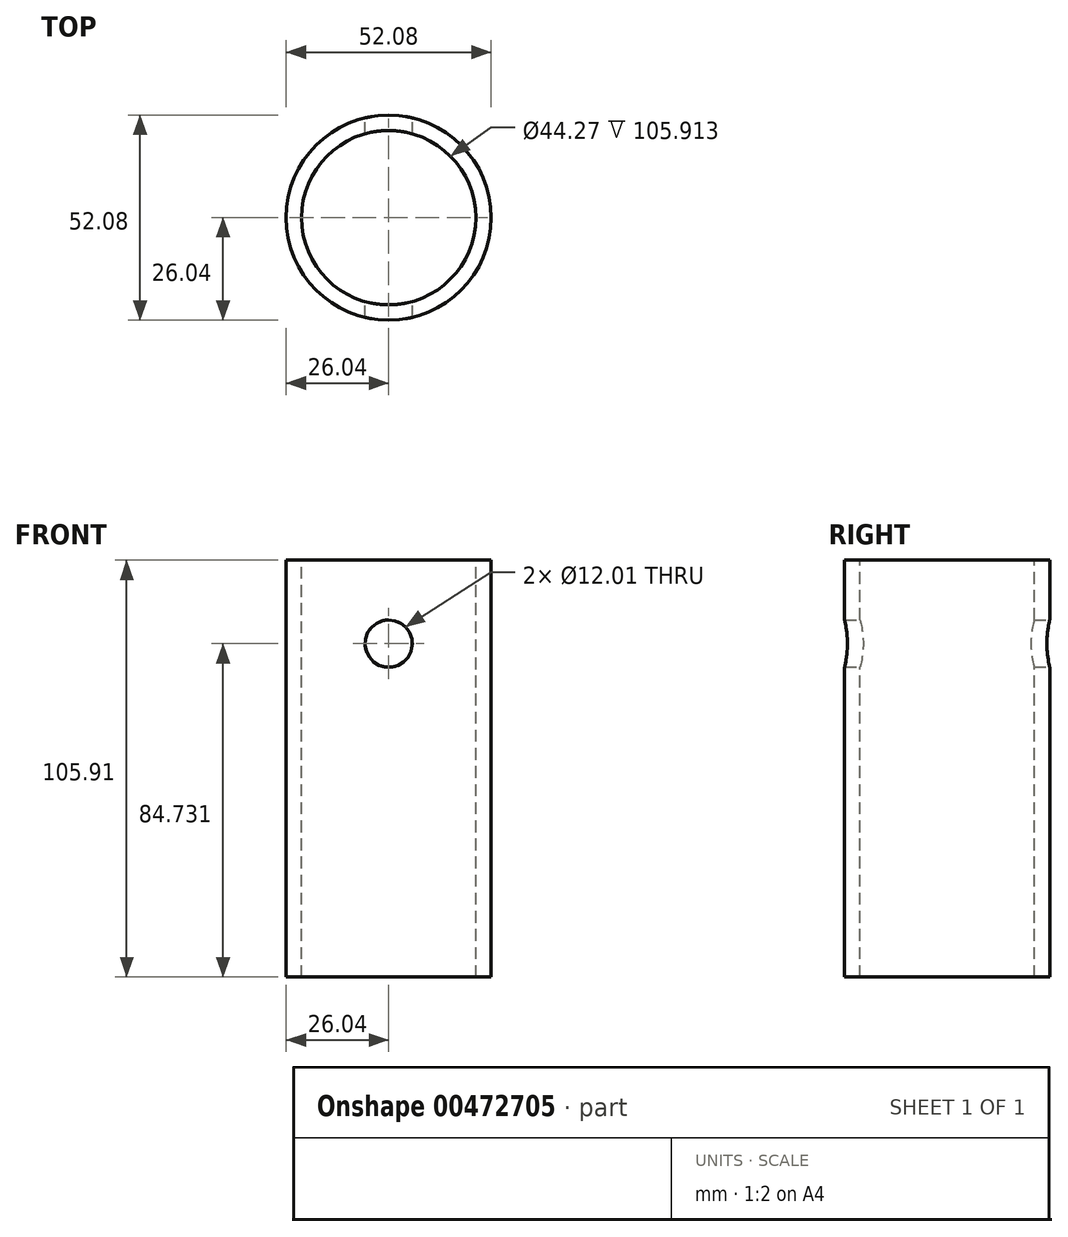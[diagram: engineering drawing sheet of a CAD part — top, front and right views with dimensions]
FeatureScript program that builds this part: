
annotation { "Feature Type Name" : "Feature", "Feature Type Description" : "" }
export const myFeature = defineFeature(function(context is Context, id is Id, definition is map)
    precondition{}
    {
        {
            var Q0;
            Q0=qCreatedBy(makeId("Top.planeOp"),FACE);
            var sketch = newSketch(context, id + "F0", { "sketchPlane" : qUnion([Q0])});
            skCircle(sketch, "E0", {"center": v(0, 0) * mm, "radius": 26.04 * mm});
            skSolve(sketch);
        }
        {
            var Q0;
            Q0 = qSketchRegion(id + "F0", true);
            extrude(context, id + "F1", {"entities" : qUnion([Q0]), "depth" : 105.9 * mm});
        }
        {
            var Q0;
            Q0=makeQuery(id+"F1.opExtrude","CAP_FACE",FACE,{"disambiguationData":[OSD([sQuery(id+"F0.wireOp",EDGE,"E0")])],"isStart":false});
            var sketch = newSketch(context, id + "F2", { "sketchPlane" : qUnion([Q0])});
            skSolve(sketch);
        }
        {
            var Q0;
            Q0=makeQuery(id+"F2.imprint","IMPRINT",FACE,{"disambiguationData":[TD([[makeQuery(id+"F2.imprint","IMPRINT",EDGE,{"derivedFrom":makeQuery(id+"F1.opExtrude","CAP_EDGE",EDGE,{"disambiguationData":[OSD([sQuery(id+"F0.wireOp",EDGE,"E0")])],"isStart":false})}),1.0]])]});
            var sketch = newSketch(context, id + "F3", { "sketchPlane" : qUnion([Q0])});
            skCircle(sketch, "E1", {"center": v(0, 0) * mm, "radius": 22.13 * mm});
            skSolve(sketch);
        }
        {
            var Q0;
            Q0 = qSketchRegion(id + "F3", true);
            var sketch = newSketch(context, id + "F4", { "sketchPlane" : qUnion([Q0])});
            skSolve(sketch);
        }
        {
            var Q0;
            Q0=makeQuery(id+"F2.imprint","IMPRINT",FACE,{"disambiguationData":[TD([[makeQuery(id+"F2.imprint","IMPRINT",EDGE,{"derivedFrom":makeQuery(id+"F1.opExtrude","CAP_EDGE",EDGE,{"disambiguationData":[OSD([sQuery(id+"F0.wireOp",EDGE,"E0")])],"isStart":false})}),1.0]])]});
            var Q1;
            Q1=makeQuery(id+"F3.imprint","IMPRINT",FACE,{"disambiguationData":[TD([[makeQuery(id+"F3.imprint","IMPRINT",EDGE,{"derivedFrom":sQuery(id+"F3.wireOp",EDGE,"E1")}),1.0]])]});
            extrude(context, id + "F5", {"entities" : qUnion([Q0, Q1]), "operationType" : NewBodyOperationType.ADD, "oppositeDirection" : true, "depth" : 88.55 * mm});
        }
        {
            var Q0;
            Q0=makeQuery(id+"F4.imprint","IMPRINT",FACE,{"disambiguationData":[TD([[makeQuery(id+"F4.imprint","IMPRINT",EDGE,{"derivedFrom":makeQuery(id+"F3.imprint","IMPRINT",EDGE,{"derivedFrom":sQuery(id+"F3.wireOp",EDGE,"E1")})}),1.0]])]});
            extrude(context, id + "F6", {"entities" : qUnion([Q0]), "operationType" : NewBodyOperationType.REMOVE, "oppositeDirection" : true, "depth" : 185.23 * mm});
        }
        {
            var Q0;
            Q0=qCreatedBy(makeId("Front.planeOp"),FACE);
            var sketch = newSketch(context, id + "F7", { "sketchPlane" : qUnion([Q0])});
            skCircle(sketch, "E2", {"center": v(0, 84.73) * mm, "radius": 6 * mm});
            skSolve(sketch);
        }
        {
            var Q0;
            Q0 = qSketchRegion(id + "F7", true);
            extrude(context, id + "F8", {"entities" : qUnion([Q0]), "operationType" : NewBodyOperationType.REMOVE, "depth" : 38.1 * mm, "hasSecondDirection" : true, "secondDirectionOppositeDirection" : true, "secondDirectionDepth" : 38.1 * mm});
        }
    });
